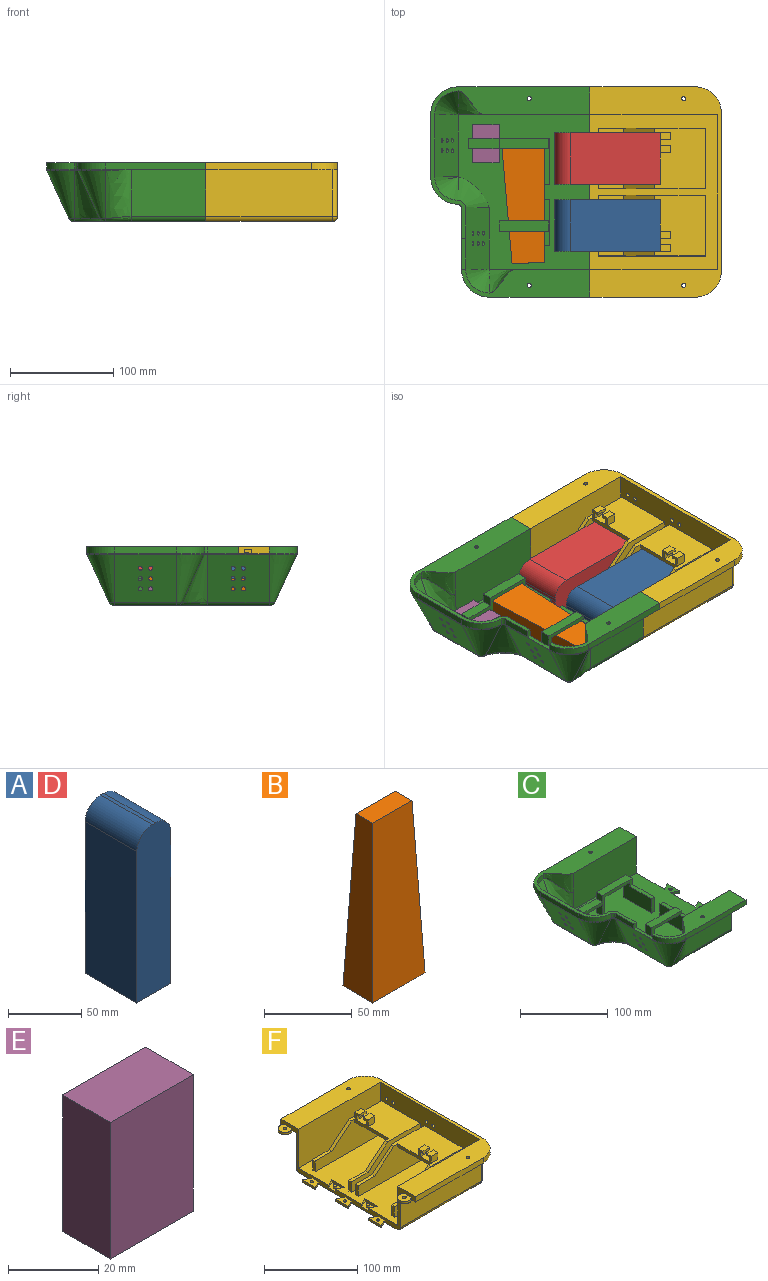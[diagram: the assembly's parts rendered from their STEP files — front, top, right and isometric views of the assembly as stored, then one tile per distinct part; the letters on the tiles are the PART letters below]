
ASSEMBLY  parts=6 mates=4
PART A: 8 faces, bbox 33x50x142 mm
  f0: plane 127x50mm, normal (1,0,0), area 6350mm2, adj f1,f3,f5,f7
  f1: plane 142x33mm, normal (0,1,0), area 4589.4mm2, adj f0,f2,f4,f5,f6,f7
  f2: plane 127x50mm, normal (-1,0,0), area 6350mm2, adj f1,f3,f5,f6
  f3: plane 142x33mm, normal (0,-1,0), area 4589.4mm2, adj f0,f2,f4,f5,f6,f7
  f4: plane 50x3mm, normal (0,0,1), area 150mm2, adj f1,f3,f6,f7
  f5: plane 50x33mm, normal (0,0,-1), area 1650mm2, adj f0,f1,f2,f3
  f6: cylinder r=15mm len=50mm, axis (0,1,0), area 1178.1mm2, adj f1,f2,f3,f4
  f7: cylinder r=15mm len=50mm, axis (0,-1,0), area 1178.1mm2, adj f0,f1,f3,f4
PART B: 6 faces, bbox 42x24x120 mm
  f0: plane 120x24mm, normal (1,0,0.04), area 2253.4mm2, adj f1,f3,f4,f5
  f1: plane 120x42mm, normal (0,1,0.04), area 4415.5mm2, adj f0,f2,f4,f5
  f2: plane 120x24mm, normal (-1,0,0.04), area 2253.4mm2, adj f1,f3,f4,f5
  f3: plane 120x42mm, normal (0,-1,0.04), area 4415.5mm2, adj f0,f2,f4,f5
  f4: plane 31.52x13.52mm, normal (0,0,1), area 426.2mm2, adj f0,f1,f2,f3
  f5: plane 42x24mm, normal (0,0,-1), area 1008mm2, adj f0,f1,f2,f3
PART C: 148 faces, bbox 170.7x212.4x61 mm
  f0: plane 204x57mm, normal (1,0,0), area 1449.1mm2, adj f1,f3,f6,f7,f9,f12,f13,f15
  f1: plane 10x5mm, normal (-0.45,-0.89,0), area 33.5mm2, adj f0,f2,f3,f147
  f2: plane 20x3mm, normal (1,0,0), area 60mm2, adj f1,f3,f6,f147
  f3: plane 20x10mm, normal (0,0,-1), area 137.4mm2, adj f0,f1,f2,f4,f6
  f4: cylinder r=2mm len=4mm, axis (0,0,1), area 37.7mm2, adj f3,f5
  f5: plane 4x4mm, normal (0,0,-1), area 12.6mm2, adj f4
  f6: plane 10x5mm, normal (-0.45,0.89,0), area 33.5mm2, adj f0,f2,f3,f147
  f7: plane 10x5mm, normal (-0.45,-0.89,0), area 33.5mm2, adj f0,f8,f9,f147
  f8: plane 20x3mm, normal (1,0,0), area 60mm2, adj f7,f9,f12,f147
  f9: plane 20x10mm, normal (0,0,-1), area 137.4mm2, adj f0,f7,f8,f10,f12
  f10: cylinder r=2mm len=4mm, axis (0,0,1), area 37.7mm2, adj f9,f11
  f11: plane 4x4mm, normal (0,0,-1), area 12.6mm2, adj f10
  f12: plane 10x5mm, normal (-0.45,0.89,0), area 33.5mm2, adj f0,f8,f9,f147
  f13: plane 10x5mm, normal (-0.45,-0.89,0), area 33.5mm2, adj f0,f14,f15,f147
  f14: plane 20x3mm, normal (1,0,0), area 60mm2, adj f13,f15,f18,f147
  f15: plane 20x10mm, normal (0,0,-1), area 137.4mm2, adj f0,f13,f14,f16,f18
  f16: cylinder r=2mm len=4mm, axis (0,0,1), area 37.7mm2, adj f15,f17
  f17: plane 4x4mm, normal (0,0,-1), area 12.6mm2, adj f16
  f18: plane 10x5mm, normal (-0.45,0.89,0), area 33.5mm2, adj f0,f14,f15,f147
  f19: cylinder r=5mm len=72.5mm, axis (-1,0,0), area 569.4mm2, adj f0,f20,f87,f147
  f20: bspline ~32.38x6.34mm, area 169.4mm2, adj f19,f21,f86,f147
  f21: torus R=0.8mm, axis (0,0,-1), area 30mm2, adj f20,f22,f85,f147
  f22: cylinder r=5mm len=60mm, axis (0,1,0), area 341.9mm2, adj f21,f23,f84,f147
  f23: bspline ~36.64x36.64mm, area 232.8mm2, adj f22,f24,f83,f147
  f24: torus R=0.8mm, axis (0,0,-1), area 30mm2, adj f23,f25,f82,f147
  f25: cylinder r=5mm len=60mm, axis (0,1,0), area 341.9mm2, adj f24,f26,f81,f147
  f26: torus R=0.8mm, axis (0,0,-1), area 30mm2, adj f25,f27,f80,f147
  f27: bspline ~37.57x6.34mm, area 169.4mm2, adj f26,f28,f146,f147
  f28: bspline ~50x25mm, area 1365.3mm2, adj f27,f29,f80,f145
  f29: bspline ~25x23mm, area 292.2mm2, adj f28,f30,f139,f144
  f30: torus R=25mm, axis (0,0,-1), area 36.5mm2, adj f29,f31,f79,f80
  f31: cylinder r=27mm len=27mm, axis (0,0,1), area 278.3mm2, adj f30,f32,f137,f139
  f32: plane 60x6.56mm, normal (-1,0,0), area 393.7mm2, adj f31,f33,f79,f137
  f33: cylinder r=27mm len=27mm, axis (0,0,-1), area 278.3mm2, adj f32,f34,f78,f137
  f34: bspline ~7x3mm, area 29.4mm2, adj f33,f35,f77,f137
  f35: plane 30x6.56mm, normal (-1,0,0), area 196.9mm2, adj f34,f36,f76,f137
  f36: plane 7x4mm, normal (0,-1,0), area 28mm2, adj f35,f37,f75,f76,f137
  f37: plane 30x3.95mm, normal (0,0,1), area 118.5mm2, adj f36,f38,f49,f76
  f38: plane 7x4mm, normal (0,1,0), area 28mm2, adj f37,f39,f40,f42,f95
  f39: cylinder r=27mm len=27mm, axis (0,0,-1), area 278.3mm2, adj f38,f40,f94,f95
  f40: torus R=25mm, axis (0,0,1), area 36.5mm2, adj f38,f39,f41,f76,f85
  f41: bspline ~25x23mm, area 292.2mm2, adj f40,f86,f92,f94
  f42: cylinder r=23mm len=23mm, axis (0,0,-1), area 252.9mm2, adj f38,f43,f48,f95
  f43: bspline ~26.5x25mm, area 586.1mm2, adj f42,f44,f95,f96
  f44: bspline ~46x25mm, area 1035.2mm2, adj f43,f45,f48,f96
  f45: plane 25.01x2.01mm, normal (0,-1,0), area 50mm2, adj f44,f46,f107
  f46: plane 60x2mm, normal (-1,0,0), area 120mm2, adj f45,f47,f49,f107
  f47: plane 2x1mm, normal (0,-1,0), area 1mm2, adj f46,f49,f107
  f48: cone r=0mm half-angle=26.6deg, axis (0,0,1), area 929mm2, adj f42,f44,f49
  f49: plane 64x50mm, normal (0.89,0,0.45), area 3001.5mm2, adj f37,f46,f47,f48,f50,f69,f70,f71
  f50: bspline ~46x30mm, area 1301.5mm2, adj f49,f51,f68,f107
  f51: bspline ~7x7mm, area 73.1mm2, adj f50,f52,f75,f137
  f52: cylinder r=23mm len=23mm, axis (0,0,-1), area 252.9mm2, adj f51,f53,f68,f137
  f53: plane 60x7mm, normal (1,0,0), area 420mm2, adj f52,f54,f67,f137
  f54: plane 64x50mm, normal (0.89,0,0.45), area 3001.5mm2, adj f53,f55,f59,f60,f61,f62,f63,f64
  f55: plane 62.43x3.43mm, normal (-1,0,0), area 121mm2, adj f54,f56,f59,f68,f107
  f56: plane 25.01x2.01mm, normal (0,1,0), area 50mm2, adj f55,f57,f107
  f57: bspline ~46x25mm, area 1035.2mm2, adj f56,f58,f60,f136
  f58: bspline ~26.5x25mm, area 586.1mm2, adj f57,f67,f136,f137
  f59: cone r=0mm half-angle=26.6deg, axis (0,0,1), area 0.1mm2, adj f54,f55
  f60: cone r=0mm half-angle=26.6deg, axis (0,0,1), area 929mm2, adj f54,f57,f67
  f61: cylinder r=2mm len=4.48mm, axis (-1,0,0), area 56.3mm2, adj f54,f81
  f62: cylinder r=2mm len=4.88mm, axis (-1,0,0), area 61.3mm2, adj f54,f81
  f63: cylinder r=2mm len=4.88mm, axis (-1,0,0), area 61.3mm2, adj f54,f81
  f64: cylinder r=2mm len=5.28mm, axis (-1,0,0), area 66.4mm2, adj f54,f81
  f65: cylinder r=2mm len=4.48mm, axis (-1,0,0), area 56.3mm2, adj f54,f81
  f66: cylinder r=2mm len=5.28mm, axis (-1,0,0), area 66.4mm2, adj f54,f81
  f67: cylinder r=23mm len=23mm, axis (0,0,1), area 252.9mm2, adj f53,f58,f60,f137
  f68: cone r=0mm half-angle=26.6deg, axis (0,0,1), area 928mm2, adj f50,f52,f54,f55
  f69: cylinder r=2mm len=5.28mm, axis (-1,0,0), area 66.4mm2, adj f49,f84
  f70: cylinder r=2mm len=4.88mm, axis (-1,0,0), area 61.3mm2, adj f49,f84
  f71: cylinder r=2mm len=4.88mm, axis (-1,0,0), area 61.3mm2, adj f49,f84
  f72: cylinder r=2mm len=4.48mm, axis (-1,0,0), area 56.3mm2, adj f49,f84
  f73: cylinder r=2mm len=5.28mm, axis (-1,0,0), area 66.4mm2, adj f49,f84
  f74: cylinder r=2mm len=4.48mm, axis (-1,0,0), area 56.3mm2, adj f49,f84
  f75: plane 30x7mm, normal (1,0,0), area 210mm2, adj f36,f49,f51,f137
  f76: cylinder r=2mm len=60mm, axis (0,-1,0), area 38.5mm2, adj f35,f36,f37,f40,f77,f84
  f77: bspline ~3.57x3.43mm, area 3.7mm2, adj f34,f76,f78,f83
  f78: torus R=25mm, axis (0,0,1), area 36.5mm2, adj f33,f77,f79,f82
  f79: cylinder r=2mm len=60mm, axis (0,-1,0), area 51.7mm2, adj f30,f32,f78,f81
  f80: cone r=4mm half-angle=24.7deg, axis (0,0,1), area 1298mm2, adj f26,f28,f30,f81
  f81: plane 63.68x50.37mm, normal (-0.91,0,-0.42), area 3000.7mm2, adj f25,f61,f62,f63,f64,f65,f66,f79
  f82: cone r=4mm half-angle=24.7deg, axis (0,0,1), area 1298mm2, adj f24,f78,f81,f83
  f83: bspline ~50x26mm, area 1053.6mm2, adj f23,f77,f82,f84
  f84: plane 63.68x50.37mm, normal (-0.91,0,-0.42), area 3000.7mm2, adj f22,f69,f70,f71,f72,f73,f74,f76
  f85: cone r=4mm half-angle=24.7deg, axis (0,0,1), area 1298mm2, adj f21,f40,f84,f86
  f86: bspline ~50x25mm, area 1365.3mm2, adj f20,f41,f85,f87
  f87: plane 72.5x45mm, normal (0,-1,0), area 3262.5mm2, adj f0,f19,f86,f92
  f88: plane 15x12.78mm, normal (0,0,-1), area 147.9mm2, adj f0,f89,f91
  f89: cylinder r=2mm len=4mm, axis (0,0,-1), area 37.7mm2, adj f88,f90
  f90: plane 4x4mm, normal (0,0,-1), area 12.6mm2, adj f89
  f91: cylinder r=7.5mm len=15mm, axis (0,0,-1), area 105.8mm2, adj f0,f88,f92
  f92: plane 72.5x23mm, normal (0,0,-1), area 1494.5mm2, adj f0,f41,f87,f91,f93,f94
  f93: cylinder r=2mm len=7mm, axis (0,0,-1), area 88mm2, adj f92,f95
  f94: plane 97.71x7.21mm, normal (0,-1,0), area 677mm2, adj f0,f39,f41,f92,f95
  f95: plane 124.5x27mm, normal (0,0,1), area 2482.7mm2, adj f0,f38,f39,f42,f43,f93,f94,f96
  f96: plane 72.5x51mm, normal (0,1,0), area 3697.5mm2, adj f0,f43,f44,f95,f107
  f97: plane 10x5mm, normal (-0.45,-0.89,0), area 33.5mm2, adj f0,f98,f99,f107
  f98: plane 20x3mm, normal (1,0,0), area 60mm2, adj f97,f99,f101,f107
  f99: plane 20x10mm, normal (0,0,-1), area 137.4mm2, adj f0,f97,f98,f100,f101
  f100: cylinder r=2mm len=4mm, axis (0,0,-1), area 37.7mm2, adj f99,f107
  f101: plane 10x5mm, normal (-0.45,0.89,0), area 33.5mm2, adj f0,f98,f99,f107
  f102: plane 10x5mm, normal (-0.45,-0.89,0), area 33.5mm2, adj f0,f103,f104,f107
  f103: plane 20x3mm, normal (1,0,0), area 60mm2, adj f102,f104,f106,f107
  f104: plane 20x10mm, normal (0,0,-1), area 137.4mm2, adj f0,f102,f103,f105,f106
  f105: cylinder r=2mm len=4mm, axis (0,0,-1), area 37.7mm2, adj f104,f107
  f106: plane 10x5mm, normal (-0.45,0.89,0), area 33.5mm2, adj f0,f103,f104,f107
  f107: plane 152.84x140.33mm, normal (0,0,1), area 16450mm2, adj f0,f45,f46,f47,f50,f55,f56,f96
  f108: plane 45x20mm, normal (-1,0,0), area 900mm2, adj f107,f109,f110,f113,f115
  f109: plane 40x10mm, normal (0,0,-1), area 400mm2, adj f108,f128,f129,f131
  f110: plane 45x5mm, normal (0,0,1), area 185mm2, adj f108,f111,f113,f114,f115,f129,f131
  f111: plane 10x4mm, normal (1,0,0), area 40mm2, adj f110,f112,f129,f131
  f112: plane 48x10mm, normal (0,0,1), area 480mm2, adj f111,f129,f130,f131
  f113: plane 20x5mm, normal (0,-1,0), area 100mm2, adj f107,f108,f110,f114
  f114: plane 45x20mm, normal (1,0,0), area 900mm2, adj f107,f110,f113,f115
  f115: plane 20x5mm, normal (0,1,0), area 100mm2, adj f107,f108,f110,f114
  f116: plane 25x10mm, normal (1,0,0), area 250mm2, adj f107,f117,f127,f134
  f117: plane 40x10mm, normal (0,0,-1), area 400mm2, adj f116,f127,f134,f135
  f118: plane 16x10mm, normal (-1,0,0), area 160mm2, adj f107,f119,f127,f134
  f119: plane 26x10mm, normal (0,0,-1), area 260mm2, adj f118,f120,f127,f134
  f120: plane 16x10mm, normal (1,0,0), area 160mm2, adj f107,f119,f127,f134
  f121: plane 20x10mm, normal (-1,0,0), area 200mm2, adj f107,f122,f127,f134
  f122: plane 30x10mm, normal (0,0,1), area 300mm2, adj f121,f123,f127,f134
  f123: plane 10x9mm, normal (-1,0,0), area 90mm2, adj f122,f124,f127,f134
  f124: plane 48x10mm, normal (0,0,1), area 480mm2, adj f123,f125,f127,f134
  f125: plane 10x9mm, normal (1,0,0), area 90mm2, adj f124,f126,f127,f134
  f126: plane 45x5mm, normal (0,0,1), area 185mm2, adj f125,f127,f132,f133,f134,f135
  f127: plane 78x29mm, normal (0,-1,0), area 496mm2, adj f107,f116,f117,f118,f119,f120,f121,f122
  f128: plane 20x10mm, normal (1,0,0), area 200mm2, adj f107,f109,f129,f131
  f129: plane 48x24mm, normal (0,1,0), area 272mm2, adj f107,f109,f110,f111,f112,f128,f130
  f130: plane 24x10mm, normal (-1,0,0), area 240mm2, adj f107,f112,f129,f131
  f131: plane 48x24mm, normal (0,-1,0), area 272mm2, adj f107,f109,f110,f111,f112,f128,f130
  f132: plane 20x5mm, normal (0,-1,0), area 100mm2, adj f107,f126,f133,f135
  f133: plane 45x20mm, normal (1,0,0), area 900mm2, adj f107,f126,f132,f134
  f134: plane 79x29mm, normal (0,1,0), area 596mm2, adj f107,f116,f117,f118,f119,f120,f121,f122
  f135: plane 45x25mm, normal (-1,0,0), area 950mm2, adj f107,f117,f126,f127,f132,f134
  f136: plane 102.5x51mm, normal (0,-1,0), area 5227.5mm2, adj f0,f57,f58,f107,f137
  f137: plane 154.5x147mm, normal (0,0,1), area 3834.9mm2, adj f0,f31,f32,f33,f34,f35,f36,f51
  f138: cylinder r=2mm len=7mm, axis (0,0,-1), area 88mm2, adj f137,f144
  f139: plane 127.71x7.21mm, normal (0,1,0), area 887mm2, adj f0,f29,f31,f137,f144
  f140: plane 15x12.78mm, normal (0,0,-1), area 147.9mm2, adj f0,f141,f143
  f141: cylinder r=2mm len=4mm, axis (0,0,-1), area 37.7mm2, adj f140,f142
  f142: plane 4x4mm, normal (0,0,-1), area 12.6mm2, adj f141
  f143: cylinder r=7.5mm len=15mm, axis (0,0,-1), area 105.8mm2, adj f0,f140,f144
  f144: plane 102.5x23mm, normal (0,0,-1), area 2184.5mm2, adj f0,f29,f138,f139,f143,f145
  f145: plane 102.5x45mm, normal (0,1,0), area 4612.5mm2, adj f0,f28,f144,f146
  f146: cylinder r=5mm len=102.5mm, axis (-1,0,0), area 805mm2, adj f0,f27,f145,f147
  f147: plane 151.59x128.3mm, normal (0,0,-1), area 16190.9mm2, adj f0,f1,f2,f6,f7,f8,f12,f13
PART D: same geometry as A
PART E: 6 faces, bbox 26x15x37 mm
  f0: plane 37x15mm, normal (1,0,0), area 555mm2, adj f1,f3,f4,f5
  f1: plane 37x26mm, normal (0,1,0), area 962mm2, adj f0,f2,f4,f5
  f2: plane 37x15mm, normal (-1,0,0), area 555mm2, adj f1,f3,f4,f5
  f3: plane 37x26mm, normal (0,-1,0), area 962mm2, adj f0,f2,f4,f5
  f4: plane 26x15mm, normal (0,0,1), area 390mm2, adj f0,f1,f2,f3
  f5: plane 26x15mm, normal (0,0,-1), area 390mm2, adj f0,f1,f2,f3
PART F: 158 faces, bbox 140.3x204x57 mm
  f0: plane 204x57mm, normal (-1,0,0), area 1449.1mm2, adj f2,f3,f5,f6,f8,f9,f11,f42
  f1: plane 20x3mm, normal (-1,0,0), area 60mm2, adj f2,f3,f5,f6
  f2: plane 10x5mm, normal (0.45,-0.89,0), area 33.5mm2, adj f0,f1,f5,f6
  f3: plane 10x5mm, normal (0.45,0.89,0), area 33.5mm2, adj f0,f1,f5,f6
  f4: cylinder r=2mm len=4mm, axis (0,0,1), area 37.7mm2, adj f5,f6
  f5: plane 148x132.5mm, normal (0,0,-1), area 18542.3mm2, adj f0,f1,f2,f3,f4,f7,f8,f9
  f6: plane 20x10mm, normal (0,0,1), area 137.4mm2, adj f0,f1,f2,f3,f4
  f7: plane 20x3mm, normal (-1,0,0), area 60mm2, adj f5,f8,f9,f11
  f8: plane 10x5mm, normal (0.45,-0.89,0), area 33.5mm2, adj f0,f5,f7,f11
  f9: plane 10x5mm, normal (0.45,0.89,0), area 33.5mm2, adj f0,f5,f7,f11
  f10: cylinder r=2mm len=4mm, axis (0,0,1), area 37.7mm2, adj f5,f11
  f11: plane 20x10mm, normal (0,0,1), area 137.4mm2, adj f0,f7,f8,f9,f10
  f12: plane 59x49.21mm, normal (0,0,1), area 2577.6mm2, adj f13,f14,f15,f17,f18,f19,f21,f22
  f13: plane 104x39mm, normal (0,1,0), area 3058.6mm2, adj f12,f19,f21,f25,f26,f42
  f14: plane 104x39mm, normal (0,-1,0), area 3058.6mm2, adj f12,f19,f22,f23,f24,f42
  f15: plane 100x39mm, normal (0,1,0), area 2742.6mm2, adj f12,f16,f18,f20,f22,f23,f24,f42
  f16: plane 51x40mm, normal (0,0,-1), area 2040mm2, adj f15,f17,f18,f20
  f17: plane 100x39mm, normal (0,-1,0), area 2742.6mm2, adj f12,f16,f18,f20,f21,f25,f26,f42
  f18: plane 51x13mm, normal (-1,0,0), area 282mm2, adj f12,f15,f16,f17,f72,f73,f74,f75
  f19: plane 59x39mm, normal (1,0,0), area 2112.5mm2, adj f12,f13,f14,f42,f122,f123,f124,f125
  f20: plane 51x35mm, normal (-1,0,0), area 1596.5mm2, adj f15,f16,f17,f42,f122,f123,f124,f125
  f21: plane 29.79x25mm, normal (-0.64,0,0.77), area 155.6mm2, adj f12,f13,f17,f25
  f22: plane 29.79x25mm, normal (-0.64,0,0.77), area 155.6mm2, adj f12,f14,f15,f23
  f23: plane 25x4mm, normal (0,0,1), area 100mm2, adj f14,f15,f22,f24
  f24: plane 14x4mm, normal (-1,0,0), area 56mm2, adj f14,f15,f23,f42
  f25: plane 25x4mm, normal (0,0,1), area 100mm2, adj f13,f17,f21,f26
  f26: plane 14x4mm, normal (-1,0,0), area 56mm2, adj f13,f17,f25,f42
  f27: plane 59x49.21mm, normal (0,0,1), area 2577.6mm2, adj f28,f29,f30,f32,f33,f34,f36,f37
  f28: plane 51x13mm, normal (-1,0,0), area 282mm2, adj f27,f30,f31,f32,f60,f61,f62,f63
  f29: plane 104x39mm, normal (0,-1,0), area 3058.6mm2, adj f27,f34,f37,f38,f39,f42
  f30: plane 100x39mm, normal (0,1,0), area 2742.6mm2, adj f27,f28,f31,f35,f37,f38,f39,f42
  f31: plane 51x40mm, normal (0,0,-1), area 2040mm2, adj f28,f30,f32,f35
  f32: plane 100x39mm, normal (0,-1,0), area 2742.6mm2, adj f27,f28,f31,f35,f36,f40,f41,f42
  f33: plane 104x39mm, normal (0,1,0), area 3058.6mm2, adj f27,f34,f36,f40,f41,f42
  f34: plane 59x39mm, normal (1,0,0), area 2112.5mm2, adj f27,f29,f33,f42,f107,f108,f109,f110
  f35: plane 51x35mm, normal (-1,0,0), area 1596.5mm2, adj f30,f31,f32,f42,f107,f108,f109,f110
  f36: plane 29.79x25mm, normal (-0.64,0,0.77), area 155.6mm2, adj f27,f32,f33,f40
  f37: plane 29.79x25mm, normal (-0.64,0,0.77), area 155.6mm2, adj f27,f29,f30,f38
  f38: plane 25x4mm, normal (0,0,1), area 100mm2, adj f29,f30,f37,f39
  f39: plane 14x4mm, normal (-1,0,0), area 56mm2, adj f29,f30,f38,f42
  f40: plane 25x4mm, normal (0,0,1), area 100mm2, adj f32,f33,f36,f41
  f41: plane 14x4mm, normal (-1,0,0), area 56mm2, adj f32,f33,f40,f42
  f42: plane 150.01x123.5mm, normal (0,0,1), area 16153.7mm2, adj f0,f13,f14,f15,f17,f19,f20,f24
  f43: plane 140.28x28mm, normal (0,0,-1), area 2939mm2, adj f0,f44,f47,f48,f49,f99,f100,f150
  f44: plane 102.5x7mm, normal (0,1,0), area 717.5mm2, adj f0,f43,f45,f49
  f45: plane 204x127.5mm, normal (0,0,1), area 7171.7mm2, adj f0,f44,f46,f48,f49,f51,f52,f54
  f46: plane 123.5x51mm, normal (0,-1,0), area 6298.5mm2, adj f0,f42,f45,f55
  f47: plane 122.5x45mm, normal (0,1,0), area 5512.5mm2, adj f0,f43,f152,f157
  f48: plane 154x52mm, normal (1,0,0), area 7377.2mm2, adj f43,f45,f49,f50,f54,f56,f57,f58
  f49: cylinder r=25mm len=25mm, axis (0,0,-1), area 274.9mm2, adj f43,f44,f45,f48
  f50: plane 140.28x28mm, normal (0,0,-1), area 2939mm2, adj f0,f48,f51,f53,f54,f96,f97,f149
  f51: plane 102.5x7mm, normal (0,-1,0), area 717.5mm2, adj f0,f45,f50,f54
  f52: plane 123.5x51mm, normal (0,1,0), area 6298.5mm2, adj f0,f42,f45,f55
  f53: plane 122.5x45mm, normal (0,-1,0), area 5512.5mm2, adj f0,f50,f151,f153
  f54: cylinder r=25mm len=25mm, axis (0,0,-1), area 274.9mm2, adj f45,f48,f50,f51
  f55: plane 150.16x51mm, normal (-1,0,0), area 7293.5mm2, adj f42,f45,f46,f52,f56,f57,f58,f59
  f56: plane 21x4mm, normal (0,1,0), area 84mm2, adj f48,f55,f57,f59
  f57: plane 10x4mm, normal (0,0,1), area 40mm2, adj f48,f55,f56,f58
  f58: plane 21x4mm, normal (0,-1,0), area 84mm2, adj f48,f55,f57,f59
  f59: plane 10x4mm, normal (0,0,-1), area 40mm2, adj f48,f55,f56,f58
  f60: plane 10x9mm, normal (0,-1,0), area 90mm2, adj f27,f28,f64,f65
  f61: plane 10x6mm, normal (0,1,0), area 60mm2, adj f27,f28,f62,f65
  f62: plane 10x4mm, normal (0,0,-1), area 40mm2, adj f28,f61,f63,f65
  f63: plane 10x3mm, normal (0,1,0), area 30mm2, adj f28,f62,f64,f65
  f64: plane 10x7mm, normal (0,0,1), area 70mm2, adj f28,f60,f63,f65
  f65: plane 9x7mm, normal (1,0,0), area 39mm2, adj f27,f60,f61,f62,f63,f64
  f66: plane 10x6mm, normal (0,-1,0), area 60mm2, adj f27,f28,f70,f71
  f67: plane 10x9mm, normal (0,1,0), area 90mm2, adj f27,f28,f68,f71
  f68: plane 10x7mm, normal (0,0,1), area 70mm2, adj f28,f67,f69,f71
  f69: plane 10x3mm, normal (0,-1,0), area 30mm2, adj f28,f68,f70,f71
  f70: plane 10x4mm, normal (0,0,-1), area 40mm2, adj f28,f66,f69,f71
  f71: plane 9x7mm, normal (1,0,0), area 39mm2, adj f27,f66,f67,f68,f69,f70
  f72: plane 10x9mm, normal (0,-1,0), area 90mm2, adj f12,f18,f76,f77
  f73: plane 10x6mm, normal (0,1,0), area 60mm2, adj f12,f18,f74,f77
  f74: plane 10x4mm, normal (0,0,-1), area 40mm2, adj f18,f73,f75,f77
  f75: plane 10x3mm, normal (0,1,0), area 30mm2, adj f18,f74,f76,f77
  f76: plane 10x7mm, normal (0,0,1), area 70mm2, adj f18,f72,f75,f77
  f77: plane 9x7mm, normal (1,0,0), area 39mm2, adj f12,f72,f73,f74,f75,f76
  f78: plane 10x6mm, normal (0,-1,0), area 60mm2, adj f12,f18,f82,f83
  f79: plane 10x9mm, normal (0,1,0), area 90mm2, adj f12,f18,f80,f83
  f80: plane 10x7mm, normal (0,0,1), area 70mm2, adj f18,f79,f81,f83
  f81: plane 10x3mm, normal (0,-1,0), area 30mm2, adj f18,f80,f82,f83
  f82: plane 10x4mm, normal (0,0,-1), area 40mm2, adj f18,f78,f81,f83
  f83: plane 9x7mm, normal (1,0,0), area 39mm2, adj f12,f78,f79,f80,f81,f82
  f84: plane 20x3mm, normal (-1,0,0), area 60mm2, adj f42,f85,f87,f88
  f85: plane 10x5mm, normal (0.45,-0.89,0), area 33.5mm2, adj f0,f42,f84,f88
  f86: cylinder r=2mm len=4mm, axis (0,0,-1), area 37.7mm2, adj f88,f94
  f87: plane 10x5mm, normal (0.45,0.89,0), area 33.5mm2, adj f0,f42,f84,f88
  f88: plane 20x10mm, normal (0,0,1), area 137.4mm2, adj f0,f84,f85,f86,f87
  f89: plane 20x3mm, normal (-1,0,0), area 60mm2, adj f42,f90,f92,f93
  f90: plane 10x5mm, normal (0.45,-0.89,0), area 33.5mm2, adj f0,f42,f89,f93
  f91: cylinder r=2mm len=4mm, axis (0,0,-1), area 37.7mm2, adj f93,f95
  f92: plane 10x5mm, normal (0.45,0.89,0), area 33.5mm2, adj f0,f42,f89,f93
  f93: plane 20x10mm, normal (0,0,1), area 137.4mm2, adj f0,f89,f90,f91,f92
  f94: plane 4x4mm, normal (0,0,1), area 12.6mm2, adj f86
  f95: plane 4x4mm, normal (0,0,1), area 12.6mm2, adj f91
  f96: cylinder r=7.5mm len=15mm, axis (0,0,-1), area 105.8mm2, adj f0,f50,f98
  f97: cylinder r=2mm len=4mm, axis (0,0,-1), area 37.7mm2, adj f50,f98
  f98: plane 15x12.78mm, normal (0,0,1), area 147.9mm2, adj f0,f96,f97
  f99: cylinder r=7.5mm len=15mm, axis (0,0,-1), area 105.8mm2, adj f0,f43,f101
  f100: cylinder r=2mm len=4mm, axis (0,0,-1), area 37.7mm2, adj f43,f101
  f101: plane 15x12.78mm, normal (0,0,1), area 147.9mm2, adj f0,f99,f100
  f102: plane 20x3mm, normal (-1,0,0), area 60mm2, adj f5,f103,f104,f106
  f103: plane 10x5mm, normal (0.45,-0.89,0), area 33.5mm2, adj f0,f5,f102,f106
  f104: plane 10x5mm, normal (0.45,0.89,0), area 33.5mm2, adj f0,f5,f102,f106
  f105: cylinder r=2mm len=4mm, axis (0,0,1), area 37.7mm2, adj f5,f106
  f106: plane 20x10mm, normal (0,0,1), area 137.4mm2, adj f0,f102,f103,f104,f105
  f107: cylinder r=2mm len=4mm, axis (-1,0,0), area 50.3mm2, adj f34,f35
  f108: cylinder r=2mm len=4mm, axis (-1,0,0), area 50.3mm2, adj f34,f35
  f109: cylinder r=2mm len=4mm, axis (-1,0,0), area 50.3mm2, adj f34,f35
  f110: cylinder r=2mm len=4mm, axis (-1,0,0), area 50.3mm2, adj f34,f35
  f111: cylinder r=2mm len=4mm, axis (-1,0,0), area 50.3mm2, adj f34,f35
  f112: cylinder r=2mm len=4mm, axis (-1,0,0), area 50.3mm2, adj f34,f35
  f113: cylinder r=2mm len=4mm, axis (-1,0,0), area 50.3mm2, adj f34,f35
  f114: cylinder r=2mm len=4mm, axis (-1,0,0), area 50.3mm2, adj f34,f35
  f115: cylinder r=2mm len=4mm, axis (-1,0,0), area 50.3mm2, adj f34,f35
  f116: cylinder r=2mm len=4mm, axis (-1,0,0), area 50.3mm2, adj f34,f35
  f117: cylinder r=2mm len=4mm, axis (-1,0,0), area 50.3mm2, adj f34,f35
  f118: cylinder r=2mm len=4mm, axis (-1,0,0), area 50.3mm2, adj f34,f35
  f119: cylinder r=2mm len=4mm, axis (-1,0,0), area 50.3mm2, adj f34,f35
  f120: cylinder r=2mm len=4mm, axis (-1,0,0), area 50.3mm2, adj f34,f35
  f121: cylinder r=2mm len=4mm, axis (-1,0,0), area 50.3mm2, adj f34,f35
  f122: cylinder r=2mm len=4mm, axis (-1,0,0), area 50.3mm2, adj f19,f20
  f123: cylinder r=2mm len=4mm, axis (-1,0,0), area 50.3mm2, adj f19,f20
  f124: cylinder r=2mm len=4mm, axis (-1,0,0), area 50.3mm2, adj f19,f20
  f125: cylinder r=2mm len=4mm, axis (-1,0,0), area 50.3mm2, adj f19,f20
  f126: cylinder r=2mm len=4mm, axis (-1,0,0), area 50.3mm2, adj f19,f20
  f127: cylinder r=2mm len=4mm, axis (-1,0,0), area 50.3mm2, adj f19,f20
  f128: cylinder r=2mm len=4mm, axis (-1,0,0), area 50.3mm2, adj f19,f20
  f129: cylinder r=2mm len=4mm, axis (-1,0,0), area 50.3mm2, adj f19,f20
  f130: cylinder r=2mm len=4mm, axis (-1,0,0), area 50.3mm2, adj f19,f20
  f131: cylinder r=2mm len=4mm, axis (-1,0,0), area 50.3mm2, adj f19,f20
  f132: cylinder r=2mm len=4mm, axis (-1,0,0), area 50.3mm2, adj f19,f20
  f133: cylinder r=2mm len=4mm, axis (-1,0,0), area 50.3mm2, adj f19,f20
  f134: cylinder r=2mm len=4mm, axis (-1,0,0), area 50.3mm2, adj f19,f20
  f135: cylinder r=2mm len=4mm, axis (-1,0,0), area 50.3mm2, adj f19,f20
  f136: cylinder r=2mm len=4mm, axis (-1,0,0), area 50.3mm2, adj f19,f20
  f137: cylinder r=2mm len=4mm, axis (-1,0,0), area 50.3mm2, adj f48,f55
  f138: cylinder r=2mm len=4mm, axis (-1,0,0), area 50.3mm2, adj f48,f55
  f139: cylinder r=2mm len=4mm, axis (-1,0,0), area 50.3mm2, adj f48,f55
  f140: cylinder r=2mm len=4mm, axis (-1,0,0), area 50.3mm2, adj f48,f55
  f141: cylinder r=2mm len=4mm, axis (-1,0,0), area 50.3mm2, adj f48,f55
  f142: cylinder r=2mm len=4mm, axis (-1,0,0), area 50.3mm2, adj f48,f55
  f143: cylinder r=2mm len=4mm, axis (-1,0,0), area 50.3mm2, adj f48,f55
  f144: cylinder r=2mm len=4mm, axis (-1,0,0), area 50.3mm2, adj f48,f55
  f145: cylinder r=2mm len=4mm, axis (-1,0,0), area 50.3mm2, adj f48,f55
  f146: cylinder r=2mm len=4mm, axis (-1,0,0), area 50.3mm2, adj f48,f55
  f147: cylinder r=2mm len=4mm, axis (-1,0,0), area 50.3mm2, adj f48,f55
  f148: cylinder r=2mm len=4mm, axis (-1,0,0), area 50.3mm2, adj f48,f55
  f149: cylinder r=2mm len=7mm, axis (0,0,-1), area 88mm2, adj f45,f50
  f150: cylinder r=2mm len=7mm, axis (0,0,-1), area 88mm2, adj f43,f45
  f151: cylinder r=5mm len=122.5mm, axis (1,0,0), area 962.1mm2, adj f0,f5,f53,f154
  f152: cylinder r=5mm len=122.5mm, axis (1,0,0), area 962.1mm2, adj f0,f5,f47,f156
  f153: cylinder r=5mm len=45mm, axis (0,0,1), area 353.4mm2, adj f48,f50,f53,f154
  f154: sphere r=5mm, area 39.3mm2, adj f151,f153,f155
  f155: cylinder r=5mm len=148mm, axis (0,1,0), area 1162.4mm2, adj f5,f48,f154,f156
  f156: sphere r=5mm, area 39.3mm2, adj f152,f155,f157
  f157: cylinder r=5mm len=45mm, axis (0,0,-1), area 353.4mm2, adj f43,f47,f48,f156
PLACE A rot(axis=(0.71,0,-0.71),180deg) t=(58.31,43.55,-103.5)mm
PLACE B rot(axis=(1,0.02,0.02),90deg) t=(-114.67,127.13,-108)mm
PLACE C t=(-49.69,76.05,-120)mm
PLACE D rot(axis=(-0.71,0,0.71),180deg) t=(58.31,108.55,-103.5)mm
PLACE E rot(axis=(-1,0,0),90deg) t=(-150.69,104.55,-112.5)mm
PLACE F t=(-49.69,76.05,-120)mm
MATE slider B.f0 <-> C.f135  axis (1,0,0) through (-93.69,128.05,-120)mm
MATE slider E.f2 <-> C.f120  axis (-1,0,0) through (-163.69,123.05,-120)mm
MATE slider A.f5 <-> F.f20  axis (1,0,0) through (58.31,43.55,-120)mm
MATE slider D.f5 <-> F.f35  axis (1,0,0) through (58.31,108.55,-120)mm
